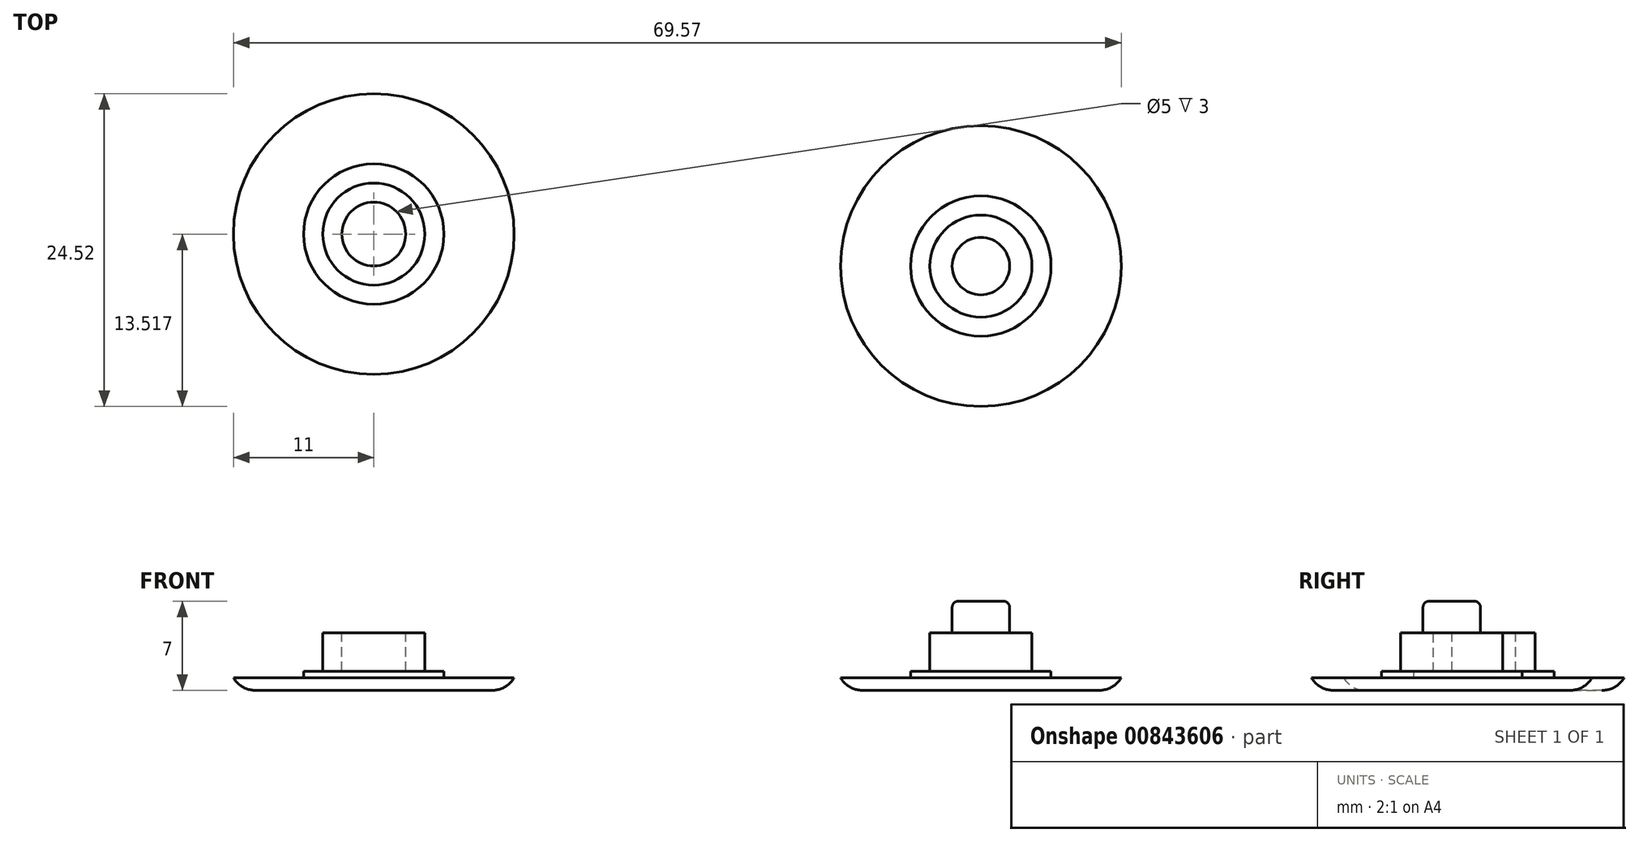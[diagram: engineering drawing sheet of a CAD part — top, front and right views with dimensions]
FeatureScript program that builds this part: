
annotation { "Feature Type Name" : "Feature", "Feature Type Description" : "" }
export const myFeature = defineFeature(function(context is Context, id is Id, definition is map)
    precondition{}
    {
        {
            var Q0;
            Q0=qCreatedBy(makeId("Top.planeOp"),FACE);
            var sketch = newSketch(context, id + "F0", { "sketchPlane" : qUnion([Q0])});
            skCircle(sketch, "E0", {"center": v(-53.7, 42.7) * mm, "radius": 11 * mm});
            skCircle(sketch, "E1", {"center": v(-6.12, 40.2) * mm, "radius": 11 * mm});
            skSolve(sketch);
        }
        {
            var Q0;
            Q0=makeQuery(id+"F0.imprint","IMPRINT",FACE,{"disambiguationData":[TD([[makeQuery(id+"F0.imprint","IMPRINT",EDGE,{"derivedFrom":sQuery(id+"F0.wireOp",EDGE,"E0")}),1.0]])]});
            var Q1;
            Q1=makeQuery(id+"F0.imprint","IMPRINT",FACE,{"disambiguationData":[TD([[makeQuery(id+"F0.imprint","IMPRINT",EDGE,{"derivedFrom":sQuery(id+"F0.wireOp",EDGE,"E1")}),1.0]])]});
            extrude(context, id + "F1", {"entities" : qUnion([Q0, Q1]), "depth" : 1 * mm, "offsetDistance" : 25 * mm});
        }
        {
            var Q0;
            Q0=makeQuery(id+"F1.opExtrude","CAP_FACE",FACE,{"disambiguationData":[OSD([sQuery(id+"F0.wireOp",EDGE,"E0")])],"isStart":false});
            var sketch = newSketch(context, id + "F2", { "sketchPlane" : qUnion([Q0])});
            skPoint(sketch, "E2", {"position": v(-53.7, 42.7) * mm});
            skCircle(sketch, "E3", {"center": v(-53.7, 42.7) * mm, "radius": 5.5 * mm});
            skSolve(sketch);
        }
        {
            var Q0;
            Q0=makeQuery(id+"F2.imprint","IMPRINT",FACE,{"disambiguationData":[TD([[makeQuery(id+"F2.imprint","IMPRINT",EDGE,{"derivedFrom":sQuery(id+"F2.wireOp",EDGE,"E3")}),1.0]])]});
            extrude(context, id + "F3", {"entities" : qUnion([Q0]), "operationType" : NewBodyOperationType.ADD, "depth" : 0.5 * mm, "offsetDistance" : 25 * mm});
        }
        {
            var Q0;
            Q0=makeQuery(id+"F3.opExtrude","CAP_FACE",FACE,{"disambiguationData":[OSD([sQuery(id+"F2.wireOp",EDGE,"E3")])],"isStart":false});
            var sketch = newSketch(context, id + "F4", { "sketchPlane" : qUnion([Q0])});
            skPoint(sketch, "E4", {"position": v(-53.7, 42.7) * mm});
            skCircle(sketch, "E5", {"center": v(-53.7, 42.7) * mm, "radius": 4 * mm});
            skSolve(sketch);
        }
        {
            var Q0;
            Q0=makeQuery(id+"F4.imprint","IMPRINT",FACE,{"disambiguationData":[TD([[makeQuery(id+"F4.imprint","IMPRINT",EDGE,{"derivedFrom":sQuery(id+"F4.wireOp",EDGE,"E5")}),1.0]])]});
            extrude(context, id + "F5", {"entities" : qUnion([Q0]), "operationType" : NewBodyOperationType.ADD, "depth" : 3 * mm, "offsetDistance" : 25 * mm});
        }
        {
            var Q0;
            Q0=makeQuery(id+"F1.opExtrude","CAP_EDGE",EDGE,{"disambiguationData":[OSD([sQuery(id+"F0.wireOp",EDGE,"E0")])],"isStart":true});
            fillet(context, id + "F6", {"entities" : qUnion([Q0]), "radius" : 2 * mm, "tangentPropagation" : true, "allowEdgeOverflow" : false});
        }
        {
            var Q0;
            Q0=makeQuery(id+"F5.opExtrude","CAP_FACE",FACE,{"disambiguationData":[OSD([sQuery(id+"F4.wireOp",EDGE,"E5")])],"isStart":false});
            var sketch = newSketch(context, id + "F7", { "sketchPlane" : qUnion([Q0])});
            skPoint(sketch, "E6", {"position": v(-53.7, 42.7) * mm});
            skCircle(sketch, "E7", {"center": v(-53.7, 42.7) * mm, "radius": 2.5 * mm});
            skSolve(sketch);
        }
        {
            var Q0;
            Q0=makeQuery(id+"F7.imprint","IMPRINT",FACE,{"disambiguationData":[TD([[makeQuery(id+"F7.imprint","IMPRINT",EDGE,{"derivedFrom":sQuery(id+"F7.wireOp",EDGE,"E7")}),1.0]])]});
            extrude(context, id + "F8", {"entities" : qUnion([Q0]), "operationType" : NewBodyOperationType.REMOVE, "oppositeDirection" : true, "depth" : 3 * mm, "offsetDistance" : 25 * mm});
        }
        {
            var Q0;
            Q0=makeQuery(id+"F1.opExtrude","CAP_FACE",FACE,{"disambiguationData":[OSD([sQuery(id+"F0.wireOp",EDGE,"E1")])],"isStart":false});
            var sketch = newSketch(context, id + "F9", { "sketchPlane" : qUnion([Q0])});
            skPoint(sketch, "E8", {"position": v(-6.12, 40.2) * mm});
            skCircle(sketch, "E9", {"center": v(-6.12, 40.2) * mm, "radius": 5.5 * mm});
            skSolve(sketch);
        }
        {
            var Q0;
            Q0=makeQuery(id+"F9.imprint","IMPRINT",FACE,{"disambiguationData":[TD([[makeQuery(id+"F9.imprint","IMPRINT",EDGE,{"derivedFrom":sQuery(id+"F9.wireOp",EDGE,"E9")}),1.0]])]});
            extrude(context, id + "F10", {"entities" : qUnion([Q0]), "operationType" : NewBodyOperationType.ADD, "depth" : 0.5 * mm, "offsetDistance" : 25 * mm});
        }
        {
            var Q0;
            Q0=makeQuery(id+"F10.opExtrude","CAP_FACE",FACE,{"disambiguationData":[OSD([sQuery(id+"F9.wireOp",EDGE,"E9")])],"isStart":false});
            var sketch = newSketch(context, id + "F11", { "sketchPlane" : qUnion([Q0])});
            skPoint(sketch, "E10", {"position": v(-6.12, 40.2) * mm});
            skCircle(sketch, "E11", {"center": v(-6.12, 40.2) * mm, "radius": 4 * mm});
            skSolve(sketch);
        }
        {
            var Q0;
            Q0=makeQuery(id+"F11.imprint","IMPRINT",FACE,{"disambiguationData":[TD([[makeQuery(id+"F11.imprint","IMPRINT",EDGE,{"derivedFrom":sQuery(id+"F11.wireOp",EDGE,"E11")}),1.0]])]});
            extrude(context, id + "F12", {"entities" : qUnion([Q0]), "operationType" : NewBodyOperationType.ADD, "depth" : 3 * mm, "offsetDistance" : 25 * mm});
        }
        {
            var Q0;
            Q0=makeQuery(id+"F12.opExtrude","CAP_FACE",FACE,{"disambiguationData":[OSD([sQuery(id+"F11.wireOp",EDGE,"E11")])],"isStart":false});
            var sketch = newSketch(context, id + "F13", { "sketchPlane" : qUnion([Q0])});
            skPoint(sketch, "E12", {"position": v(-6.12, 40.2) * mm});
            skCircle(sketch, "E13", {"center": v(-6.12, 40.2) * mm, "radius": 2.25 * mm});
            skSolve(sketch);
        }
        {
            var Q0;
            Q0=makeQuery(id+"F13.imprint","IMPRINT",FACE,{"disambiguationData":[TD([[makeQuery(id+"F13.imprint","IMPRINT",EDGE,{"derivedFrom":sQuery(id+"F13.wireOp",EDGE,"E13")}),1.0]])]});
            extrude(context, id + "F14", {"entities" : qUnion([Q0]), "operationType" : NewBodyOperationType.ADD, "depth" : 2.5 * mm, "offsetDistance" : 25 * mm});
        }
        {
            var Q0;
            Q0=makeQuery(id+"F14.opExtrude","CAP_FACE",FACE,{"disambiguationData":[OSD([sQuery(id+"F13.wireOp",EDGE,"E13")])],"isStart":false});
            var Q1;
            Q1=makeQuery(id+"F8.boolean.opBoolean","COPY",EDGE,{"derivedFrom":makeQuery(id+"F8.opExtrude","CAP_EDGE",EDGE,{"disambiguationData":[OSD([sQuery(id+"F7.wireOp",EDGE,"E7")])],"isStart":true})});
            fillet(context, id + "F15", {"entities" : qUnion([Q0, Q1]), "radius" : 0.5 * mm, "tangentPropagation" : true, "allowEdgeOverflow" : false});
        }
        {
            var Q0;
            Q0=makeQuery(id+"F1.opExtrude","CAP_FACE",FACE,{"disambiguationData":[OSD([sQuery(id+"F0.wireOp",EDGE,"E1")])],"isStart":true});
            fillet(context, id + "F16", {"entities" : qUnion([Q0]), "radius" : 2 * mm, "tangentPropagation" : true, "allowEdgeOverflow" : false});
        }
    });
